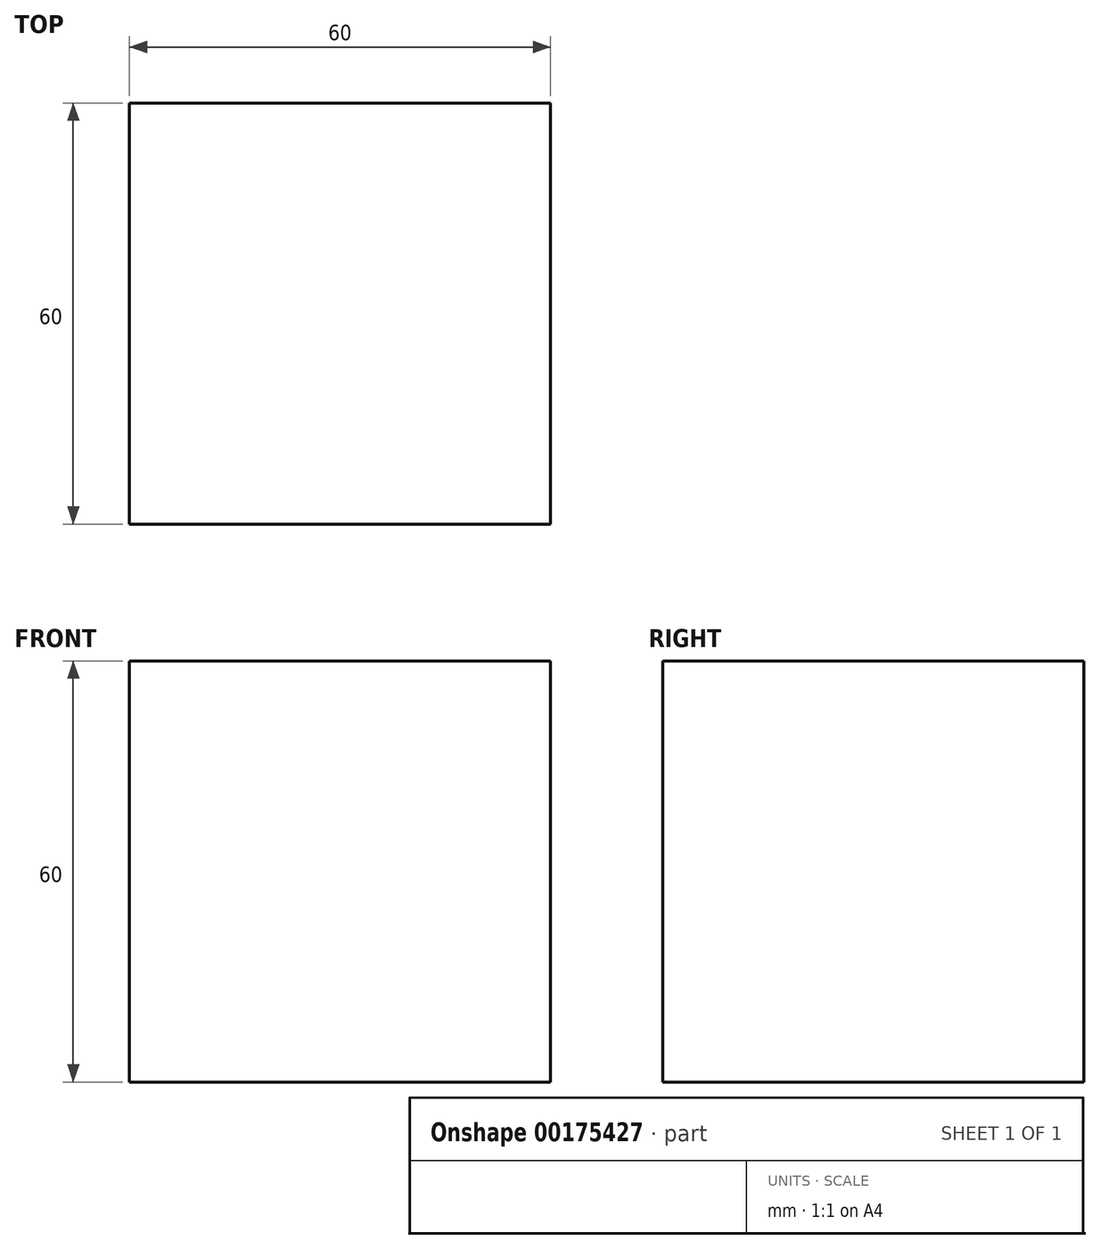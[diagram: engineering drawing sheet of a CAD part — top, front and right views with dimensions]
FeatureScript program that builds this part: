
annotation { "Feature Type Name" : "Feature", "Feature Type Description" : "" }
export const myFeature = defineFeature(function(context is Context, id is Id, definition is map)
    precondition{}
    {
        {
            var Q0;
            Q0=qCreatedBy(makeId("Top.planeOp"),FACE);
            var sketch = newSketch(context, id + "F0", { "sketchPlane" : qUnion([Q0])});
            skLineSegment(sketch, "E0.bottom", {"start": v(-34.62, 51.8) * mm, "end": v(25.38, 51.8) * mm});
            skLineSegment(sketch, "E0.top", {"start": v(-34.62, -8.2) * mm, "end": v(25.38, -8.2) * mm});
            skLineSegment(sketch, "E0.left", {"start": v(-34.62, 51.8) * mm, "end": v(-34.62, -8.2) * mm});
            skLineSegment(sketch, "E0.right", {"start": v(25.38, 51.8) * mm, "end": v(25.38, -8.2) * mm});
            skSolve(sketch);
        }
        {
            var Q0;
            Q0=makeQuery(id+"F0.imprint","IMPRINT",FACE,{"disambiguationData":[TD([[makeQuery(id+"F0.imprint","IMPRINT",EDGE,{"derivedFrom":sQuery(id+"F0.wireOp",EDGE,"E0.bottom")}),-1.0]])]});
            extrude(context, id + "F1", {"entities" : qUnion([Q0]), "depth" : 60 * mm});
        }
    });
